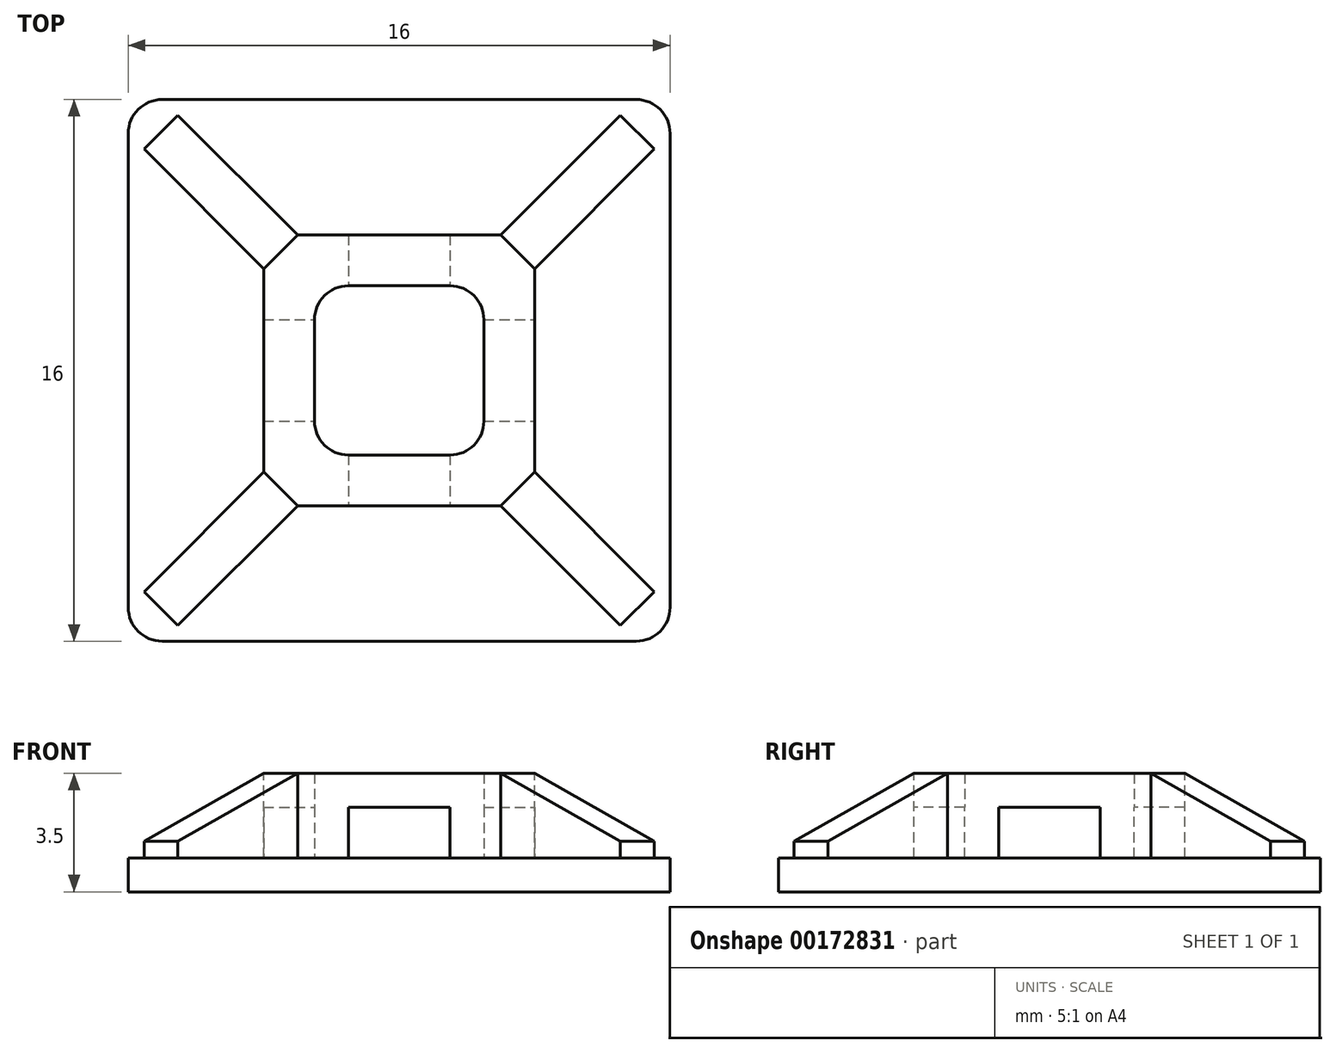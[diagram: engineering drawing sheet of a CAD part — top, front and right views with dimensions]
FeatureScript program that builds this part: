
annotation { "Feature Type Name" : "Feature", "Feature Type Description" : "" }
export const myFeature = defineFeature(function(context is Context, id is Id, definition is map)
    precondition{}
    {
        {
            var Q0;
            Q0=qCreatedBy(makeId("Top.planeOp"),FACE);
            var sketch = newSketch(context, id + "F0", { "sketchPlane" : qUnion([Q0])});
            skLineSegment(sketch, "E0.bottom", {"start": v(-8, 8) * mm, "end": v(8, 8) * mm});
            skLineSegment(sketch, "E0.top", {"start": v(-8, -8) * mm, "end": v(8, -8) * mm});
            skLineSegment(sketch, "E0.left", {"start": v(-8, 8) * mm, "end": v(-8, -8) * mm});
            skLineSegment(sketch, "E0.right", {"start": v(8, 8) * mm, "end": v(8, -8) * mm});
            skPoint(sketch, "E0.middle", {"position": v(0, 0) * mm});
            skSolve(sketch);
        }
        {
            var Q0;
            Q0=makeQuery(id+"F0.imprint","IMPRINT",FACE,{"disambiguationData":[TD([[makeQuery(id+"F0.imprint","IMPRINT",EDGE,{"derivedFrom":sQuery(id+"F0.wireOp",EDGE,"E0.bottom")}),-1.0]])]});
            extrude(context, id + "F1", {"entities" : qUnion([Q0]), "depth" : 1 * mm});
        }
        {
            var Q0;
            Q0=makeQuery(id+"F1.opExtrude","CAP_FACE",FACE,{"disambiguationData":[OSD([sQuery(id+"F0.wireOp",EDGE,"E0.bottom"),sQuery(id+"F0.wireOp",EDGE,"E0.top"),sQuery(id+"F0.wireOp",EDGE,"E0.left"),sQuery(id+"F0.wireOp",EDGE,"E0.right")])],"isStart":false});
            var sketch = newSketch(context, id + "F2", { "sketchPlane" : qUnion([Q0])});
            skLineSegment(sketch, "E1.bottom", {"start": v(-4, 4) * mm, "end": v(4, 4) * mm});
            skLineSegment(sketch, "E1.top", {"start": v(-4, -4) * mm, "end": v(4, -4) * mm});
            skLineSegment(sketch, "E1.left", {"start": v(-4, 4) * mm, "end": v(-4, -4) * mm});
            skLineSegment(sketch, "E1.right", {"start": v(4, 4) * mm, "end": v(4, -4) * mm});
            skPoint(sketch, "E1.middle", {"position": v(0, 0) * mm});
            skLineSegment(sketch, "E2.0", {"start": v(-2.5, 2.5) * mm, "end": v(2.5, 2.5) * mm});
            skLineSegment(sketch, "E2.1", {"start": v(-2.5, 2.5) * mm, "end": v(-2.5, -2.5) * mm});
            skLineSegment(sketch, "E2.2", {"start": v(-2.5, -2.5) * mm, "end": v(2.5, -2.5) * mm});
            skLineSegment(sketch, "E2.3", {"start": v(2.5, 2.5) * mm, "end": v(2.5, -2.5) * mm});
            skSolve(sketch);
        }
        {
            var Q0;
            Q0 = qSketchRegion(id + "F2", true);
            extrude(context, id + "F3", {"entities" : qUnion([Q0]), "operationType" : NewBodyOperationType.ADD, "depth" : 2.5 * mm});
        }
        {
            var Q0;
            Q0=makeQuery(id+"F3.opExtrude","SWEPT_EDGE",EDGE,{"disambiguationData":[OSD([sQuery(id+"F2.wireOp",EDGE,"E1.bottom"),sQuery(id+"F2.wireOp",EDGE,"E1.right")])]});
            var Q1;
            Q1=makeQuery(id+"F3.opExtrude","SWEPT_EDGE",EDGE,{"disambiguationData":[OSD([sQuery(id+"F2.wireOp",EDGE,"E1.bottom"),sQuery(id+"F2.wireOp",EDGE,"E1.left")])]});
            var Q2;
            Q2=makeQuery(id+"F3.opExtrude","SWEPT_EDGE",EDGE,{"disambiguationData":[OSD([sQuery(id+"F2.wireOp",EDGE,"E1.top"),sQuery(id+"F2.wireOp",EDGE,"E1.left")])]});
            var Q3;
            Q3=makeQuery(id+"F3.opExtrude","SWEPT_EDGE",EDGE,{"disambiguationData":[OSD([sQuery(id+"F2.wireOp",EDGE,"E1.top"),sQuery(id+"F2.wireOp",EDGE,"E1.right")])]});
            chamfer(context, id + "F4", {"entities" : qUnion([Q0, Q1, Q2, Q3]), "width" : 1 * mm, "tangentPropagation" : true});
        }
        {
            var Q0;
            Q0=makeQuery(id+"F4.opChamfer","BLEND_FACE",FACE,{"disambiguationData":[OSD([sQuery(id+"F2.wireOp",EDGE,"E1.top"),sQuery(id+"F2.wireOp",EDGE,"E1.left")])]});
            extrude(context, id + "F5", {"entities" : qUnion([Q0]), "operationType" : NewBodyOperationType.ADD, "depth" : 5 * mm});
        }
        {
            var Q0;
            Q0=makeQuery(id+"F4.opChamfer","BLEND_FACE",FACE,{"disambiguationData":[OSD([sQuery(id+"F2.wireOp",EDGE,"E1.top"),sQuery(id+"F2.wireOp",EDGE,"E1.right")])]});
            extrude(context, id + "F6", {"entities" : qUnion([Q0]), "operationType" : NewBodyOperationType.ADD, "depth" : 5 * mm});
        }
        {
            var Q0;
            Q0=makeQuery(id+"F4.opChamfer","BLEND_FACE",FACE,{"disambiguationData":[OSD([sQuery(id+"F2.wireOp",EDGE,"E1.bottom"),sQuery(id+"F2.wireOp",EDGE,"E1.left")])]});
            extrude(context, id + "F7", {"entities" : qUnion([Q0]), "operationType" : NewBodyOperationType.ADD, "depth" : 5 * mm});
        }
        {
            var Q0;
            Q0=makeQuery(id+"F4.opChamfer","BLEND_FACE",FACE,{"disambiguationData":[OSD([sQuery(id+"F2.wireOp",EDGE,"E1.bottom"),sQuery(id+"F2.wireOp",EDGE,"E1.right")])]});
            extrude(context, id + "F8", {"entities" : qUnion([Q0]), "operationType" : NewBodyOperationType.ADD, "depth" : 5 * mm});
        }
        {
            var Q0;
            Q0=makeQuery(id+"F8.opExtrude","CAP_EDGE",EDGE,{"disambiguationData":[OSD([sQuery(id+"F2.wireOp",EDGE,"E1.bottom"),sQuery(id+"F2.wireOp",EDGE,"E1.top"),sQuery(id+"F2.wireOp",EDGE,"E1.left"),sQuery(id+"F2.wireOp",EDGE,"E1.right"),sQuery(id+"F2.wireOp",EDGE,"E2.0"),sQuery(id+"F2.wireOp",EDGE,"E2.1"),sQuery(id+"F2.wireOp",EDGE,"E2.2"),sQuery(id+"F2.wireOp",EDGE,"E2.3")])],"isStart":false});
            var Q1;
            Q1=makeQuery(id+"F7.opExtrude","CAP_EDGE",EDGE,{"disambiguationData":[OSD([sQuery(id+"F2.wireOp",EDGE,"E1.bottom"),sQuery(id+"F2.wireOp",EDGE,"E1.top"),sQuery(id+"F2.wireOp",EDGE,"E1.left"),sQuery(id+"F2.wireOp",EDGE,"E1.right"),sQuery(id+"F2.wireOp",EDGE,"E2.0"),sQuery(id+"F2.wireOp",EDGE,"E2.1"),sQuery(id+"F2.wireOp",EDGE,"E2.2"),sQuery(id+"F2.wireOp",EDGE,"E2.3")])],"isStart":false});
            var Q2;
            Q2=makeQuery(id+"F5.opExtrude","CAP_EDGE",EDGE,{"disambiguationData":[OSD([sQuery(id+"F2.wireOp",EDGE,"E1.bottom"),sQuery(id+"F2.wireOp",EDGE,"E1.top"),sQuery(id+"F2.wireOp",EDGE,"E1.left"),sQuery(id+"F2.wireOp",EDGE,"E1.right"),sQuery(id+"F2.wireOp",EDGE,"E2.0"),sQuery(id+"F2.wireOp",EDGE,"E2.1"),sQuery(id+"F2.wireOp",EDGE,"E2.2"),sQuery(id+"F2.wireOp",EDGE,"E2.3")])],"isStart":false});
            var Q3;
            Q3=makeQuery(id+"F6.opExtrude","CAP_EDGE",EDGE,{"disambiguationData":[OSD([sQuery(id+"F2.wireOp",EDGE,"E1.bottom"),sQuery(id+"F2.wireOp",EDGE,"E1.top"),sQuery(id+"F2.wireOp",EDGE,"E1.left"),sQuery(id+"F2.wireOp",EDGE,"E1.right"),sQuery(id+"F2.wireOp",EDGE,"E2.0"),sQuery(id+"F2.wireOp",EDGE,"E2.1"),sQuery(id+"F2.wireOp",EDGE,"E2.2"),sQuery(id+"F2.wireOp",EDGE,"E2.3")])],"isStart":false});
            chamfer(context, id + "F9", {"entities" : qUnion([Q0, Q1, Q2, Q3]), "chamferType" : ChamferType.TWO_OFFSETS, "width1" : 5 * mm, "oppositeDirection" : false, "width2" : 2 * mm, "tangentPropagation" : true});
        }
        {
            var Q0;
            Q0=qCreatedBy(makeId("Front.planeOp"),FACE);
            var sketch = newSketch(context, id + "F10", { "sketchPlane" : qUnion([Q0])});
            skLineSegment(sketch, "E3.bottom", {"start": v(-1.5, 2.5) * mm, "end": v(1.5, 2.5) * mm});
            skLineSegment(sketch, "E3.top", {"start": v(-1.5, 1) * mm, "end": v(1.5, 1) * mm});
            skLineSegment(sketch, "E3.left", {"start": v(-1.5, 2.5) * mm, "end": v(-1.5, 1) * mm});
            skLineSegment(sketch, "E3.right", {"start": v(1.5, 2.5) * mm, "end": v(1.5, 1) * mm});
            skPoint(sketch, "E3.middle", {"position": v(0, 1.75) * mm});
            skSolve(sketch);
        }
        {
            var Q0;
            Q0 = qSketchRegion(id + "F10", true);
            extrude(context, id + "F11", {"entities" : qUnion([Q0]), "operationType" : NewBodyOperationType.REMOVE, "endBound" : BoundingType.THROUGH_ALL, "oppositeDirection" : true, "depth" : 25 * mm, "hasSecondDirection" : true, "secondDirectionBound" : SecondDirectionBoundingType.THROUGH_ALL, "secondDirectionOppositeDirection" : false, "secondDirectionDepth" : 25 * mm});
        }
        {
            var Q0;
            Q0=qCreatedBy(makeId("Right.planeOp"),FACE);
            var sketch = newSketch(context, id + "F12", { "sketchPlane" : qUnion([Q0])});
            skLineSegment(sketch, "E4.bottom", {"start": v(-1.5, 2.5) * mm, "end": v(1.5, 2.5) * mm});
            skLineSegment(sketch, "E4.top", {"start": v(-1.5, 1) * mm, "end": v(1.5, 1) * mm});
            skLineSegment(sketch, "E4.left", {"start": v(-1.5, 2.5) * mm, "end": v(-1.5, 1) * mm});
            skLineSegment(sketch, "E4.right", {"start": v(1.5, 2.5) * mm, "end": v(1.5, 1) * mm});
            skPoint(sketch, "E4.middle", {"position": v(0, 1.75) * mm});
            skSolve(sketch);
        }
        {
            var Q0;
            Q0 = qSketchRegion(id + "F12", true);
            extrude(context, id + "F13", {"entities" : qUnion([Q0]), "operationType" : NewBodyOperationType.REMOVE, "endBound" : BoundingType.THROUGH_ALL, "oppositeDirection" : true, "depth" : 25 * mm, "hasSecondDirection" : true, "secondDirectionBound" : SecondDirectionBoundingType.THROUGH_ALL, "secondDirectionOppositeDirection" : false, "secondDirectionDepth" : 25 * mm});
        }
        {
            var Q0;
            Q0=makeQuery(id+"F3.opExtrude","SWEPT_EDGE",EDGE,{"disambiguationData":[OSD([sQuery(id+"F2.wireOp",EDGE,"E2.0"),sQuery(id+"F2.wireOp",EDGE,"E2.1")])]});
            var Q1;
            Q1=makeQuery(id+"F3.opExtrude","SWEPT_EDGE",EDGE,{"disambiguationData":[OSD([sQuery(id+"F2.wireOp",EDGE,"E2.1"),sQuery(id+"F2.wireOp",EDGE,"E2.2")])]});
            var Q2;
            Q2=makeQuery(id+"F3.opExtrude","SWEPT_EDGE",EDGE,{"disambiguationData":[OSD([sQuery(id+"F2.wireOp",EDGE,"E2.0"),sQuery(id+"F2.wireOp",EDGE,"E2.3")])]});
            var Q3;
            Q3=makeQuery(id+"F3.opExtrude","SWEPT_EDGE",EDGE,{"disambiguationData":[OSD([sQuery(id+"F2.wireOp",EDGE,"E2.2"),sQuery(id+"F2.wireOp",EDGE,"E2.3")])]});
            var Q4;
            Q4=makeQuery(id+"F1.opExtrude","SWEPT_EDGE",EDGE,{"disambiguationData":[OSD([sQuery(id+"F0.wireOp",EDGE,"E0.top"),sQuery(id+"F0.wireOp",EDGE,"E0.right")])]});
            var Q5;
            Q5=makeQuery(id+"F1.opExtrude","SWEPT_EDGE",EDGE,{"disambiguationData":[OSD([sQuery(id+"F0.wireOp",EDGE,"E0.bottom"),sQuery(id+"F0.wireOp",EDGE,"E0.right")])]});
            var Q6;
            Q6=makeQuery(id+"F1.opExtrude","SWEPT_EDGE",EDGE,{"disambiguationData":[OSD([sQuery(id+"F0.wireOp",EDGE,"E0.top"),sQuery(id+"F0.wireOp",EDGE,"E0.left")])]});
            var Q7;
            Q7=makeQuery(id+"F1.opExtrude","SWEPT_EDGE",EDGE,{"disambiguationData":[OSD([sQuery(id+"F0.wireOp",EDGE,"E0.bottom"),sQuery(id+"F0.wireOp",EDGE,"E0.left")])]});
            fillet(context, id + "F14", {"entities" : qUnion([Q0, Q1, Q2, Q3, Q4, Q5, Q6, Q7]), "radius" : 1 * mm, "tangentPropagation" : true, "allowEdgeOverflow" : false});
        }
    });
